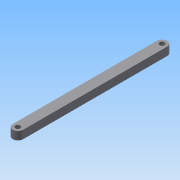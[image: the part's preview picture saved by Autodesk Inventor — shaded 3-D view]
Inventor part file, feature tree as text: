
AUTODESK INVENTOR PART (.ipt)
format: ipt  version: 2015 (Build 190159000, 159)  size: 75,264 bytes
history: native  units: mm
features: other x1, extrude x1, sketch x1
ambient origin geometry x8: Origin, YZ Plane, XZ Plane, XY Plane, X Axis, Y Axis, Z Axis, Center Point
bodies: Body1 (feature_tree)
feature tree (3):
  other  "實體1"
  extrude  "擠出1"  Depth=35.42mm
  sketch  "草圖1"
